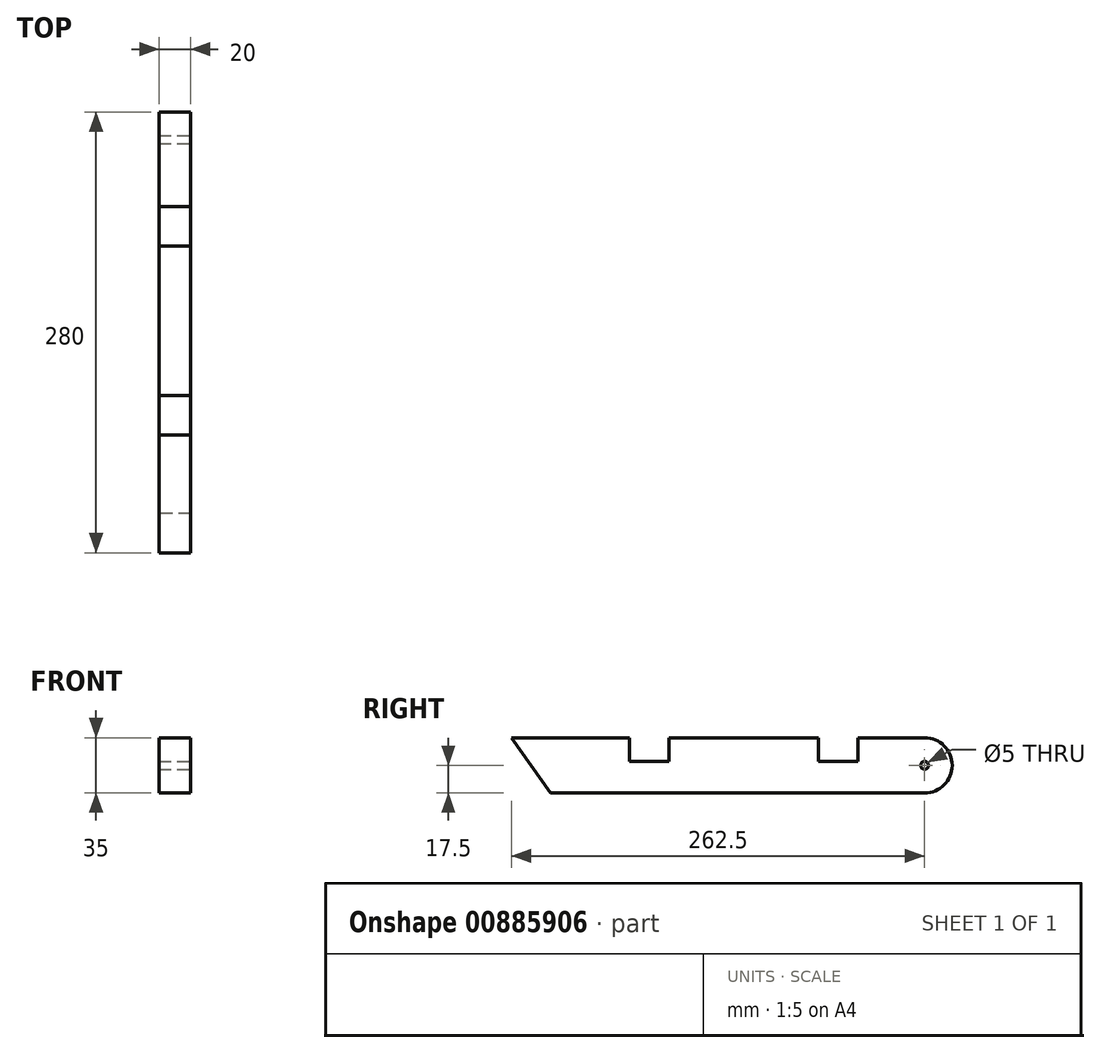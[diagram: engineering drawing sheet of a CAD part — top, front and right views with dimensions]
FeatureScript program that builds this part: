
annotation { "Feature Type Name" : "Feature", "Feature Type Description" : "" }
export const myFeature = defineFeature(function(context is Context, id is Id, definition is map)
    precondition{}
    {
        {
            var Q0;
            Q0=qCreatedBy(makeId("Right.planeOp"),FACE);
            var sketch = newSketch(context, id + "F0", { "sketchPlane" : qUnion([Q0])});
            skLineSegment(sketch, "E0.bottom", {"start": v(122.5, 17.5) * mm, "end": v(-140, 17.5) * mm});
            skLineSegment(sketch, "E0.top", {"start": v(122.5, -17.5) * mm, "end": v(-115, -17.5) * mm});
            skPoint(sketch, "E0.middle", {"position": v(0, 0) * mm});
            skArc(sketch, "E1", {"start": v(122.5, -17.5) * mm, "mid": v(140, 0) * mm, "end": v(122.5, 17.5) * mm});
            skLineSegment(sketch, "E2", {"start": v(-140, 17.5) * mm, "end": v(-115, -17.5) * mm});
            skPoint(sketch, "E3.end.orphan", {"position": v(-140, -17.5) * mm});
            skPoint(sketch, "E4.orphan", {"position": v(140, 17.5) * mm});
            skPoint(sketch, "E5.orphan", {"position": v(140, -17.5) * mm});
            skSolve(sketch);
        }
        {
            var Q0;
            Q0 = qSketchRegion(id + "F0", true);
            extrude(context, id + "F1", {"entities" : qUnion([Q0]), "depth" : 20 * mm, "offsetDistance" : 25 * mm});
        }
        {
            var Q0;
            Q0=makeQuery(id+"F1.opExtrude","CAP_FACE",FACE,{"disambiguationData":[OSD([sQuery(id+"F0.wireOp",EDGE,"E0.bottom"),sQuery(id+"F0.wireOp",EDGE,"E0.top"),sQuery(id+"F0.wireOp",EDGE,"E1"),sQuery(id+"F0.wireOp",EDGE,"E2")])],"isStart":false});
            var sketch = newSketch(context, id + "F2", { "sketchPlane" : qUnion([Q0])});
            skLineSegment(sketch, "E6.bottom", {"start": v(-65, 17.5) * mm, "end": v(-40, 17.5) * mm});
            skLineSegment(sketch, "E6.top", {"start": v(-65, 2.5) * mm, "end": v(-40, 2.5) * mm});
            skLineSegment(sketch, "E6.left", {"start": v(-65, 17.5) * mm, "end": v(-65, 2.5) * mm});
            skLineSegment(sketch, "E6.right", {"start": v(-40, 17.5) * mm, "end": v(-40, 2.5) * mm});
            skLineSegment(sketch, "E7.bottom", {"start": v(55, 17.5) * mm, "end": v(80, 17.5) * mm});
            skLineSegment(sketch, "E7.top", {"start": v(55, 2.5) * mm, "end": v(80, 2.5) * mm});
            skLineSegment(sketch, "E7.left", {"start": v(55, 17.5) * mm, "end": v(55, 2.5) * mm});
            skLineSegment(sketch, "E7.right", {"start": v(80, 17.5) * mm, "end": v(80, 2.5) * mm});
            skSolve(sketch);
        }
        {
            var Q0;
            Q0 = qSketchRegion(id + "F2", true);
            extrude(context, id + "F3", {"entities" : qUnion([Q0]), "operationType" : NewBodyOperationType.REMOVE, "oppositeDirection" : true, "depth" : 20 * mm, "offsetDistance" : 25 * mm});
        }
        {
            var Q0;
            Q0=makeQuery(id+"F1.opExtrude","CAP_FACE",FACE,{"disambiguationData":[OSD([sQuery(id+"F0.wireOp",EDGE,"E0.bottom"),sQuery(id+"F0.wireOp",EDGE,"E0.top"),sQuery(id+"F0.wireOp",EDGE,"E1"),sQuery(id+"F0.wireOp",EDGE,"E2")])],"isStart":false});
            var sketch = newSketch(context, id + "F4", { "sketchPlane" : qUnion([Q0])});
            skCircle(sketch, "E8", {"center": v(122.5, 0) * mm, "radius": 2.5 * mm});
            skSolve(sketch);
        }
        {
            var Q0;
            Q0 = qSketchRegion(id + "F4", true);
            extrude(context, id + "F5", {"entities" : qUnion([Q0]), "operationType" : NewBodyOperationType.REMOVE, "oppositeDirection" : true, "depth" : 20 * mm, "offsetDistance" : 25 * mm});
        }
    });
